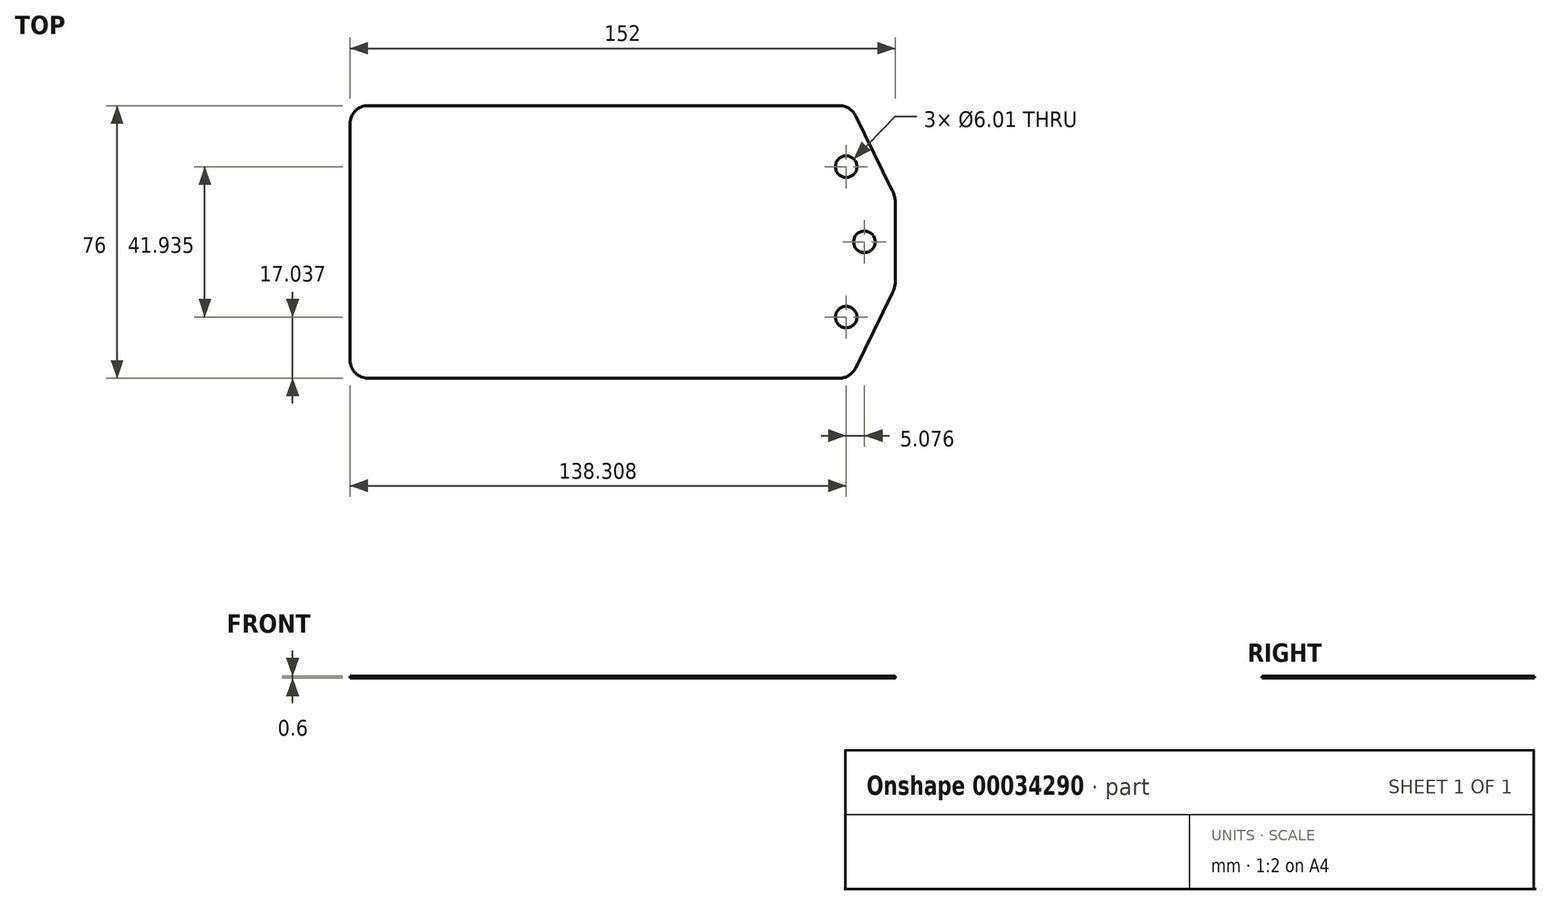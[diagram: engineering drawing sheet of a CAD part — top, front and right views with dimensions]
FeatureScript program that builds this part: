
annotation { "Feature Type Name" : "Feature", "Feature Type Description" : "" }
export const myFeature = defineFeature(function(context is Context, id is Id, definition is map)
    precondition{}
    {
        {
            var Q0;
            Q0=qCreatedBy(makeId("Top.planeOp"),FACE);
            var sketch = newSketch(context, id + "F0", { "sketchPlane" : qUnion([Q0])});
            skLineSegment(sketch, "E0.top", {"start": v(-72.18, -41.45) * mm, "end": v(59.23, -41.45) * mm});
            skLineSegment(sketch, "E0.left", {"start": v(-77.18, -3.45) * mm, "end": v(-77.18, -36.45) * mm});
            skPoint(sketch, "E1", {"position": v(62.34, -41.45) * mm});
            skPoint(sketch, "E2", {"position": v(74.82, -16.11) * mm});
            skPoint(sketch, "E3", {"position": v(-77.18, -3.45) * mm});
            skLineSegment(sketch, "E4", {"start": v(-77.18, -3.45) * mm, "end": v(92.62, -3.45) * mm, "construction": true});
            skLineSegment(sketch, "E5", {"start": v(63.72, -38.65) * mm, "end": v(74, -17.78) * mm});
            skLineSegment(sketch, "E6", {"start": v(74.82, -14.25) * mm, "end": v(74.82, -3.45) * mm});
            skPoint(sketch, "E7.visualSharp", {"position": v(-77.18, -41.45) * mm});
            skArc(sketch, "E7.filletArc", {"start": v(-77.18, -36.45) * mm, "mid": v(-75.72, -39.98) * mm, "end": v(-72.18, -41.45) * mm});
            skArc(sketch, "E8.filletArc", {"start": v(59.23, -41.45) * mm, "mid": v(61.87, -40.7) * mm, "end": v(63.72, -38.65) * mm});
            skArc(sketch, "E9.filletArc", {"start": v(74, -17.78) * mm, "mid": v(74.6, -16.06) * mm, "end": v(74.82, -14.25) * mm});
            skPoint(sketch, "E10", {"position": v(68.86, -28.22) * mm});
            skLineSegment(sketch, "E11", {"start": v(68.86, -28.22) * mm, "end": v(38.43, -13.23) * mm, "construction": true});
            skCircle(sketch, "E12", {"center": v(61.13, -24.41) * mm, "radius": 3 * mm});
            skCircle(sketch, "E13", {"center": v(66.2, -3.45) * mm, "radius": 3 * mm});
            skLineSegment(sketch, "E14.MirrorCS", {"start": v(-77.18, -3.45) * mm, "end": v(-77.18, 29.55) * mm});
            skArc(sketch, "E15.MirrorCS", {"start": v(-77.18, 29.55) * mm, "mid": v(-75.72, 33.09) * mm, "end": v(-72.18, 34.55) * mm});
            skLineSegment(sketch, "E16.MirrorCS", {"start": v(-72.18, 34.55) * mm, "end": v(59.23, 34.55) * mm});
            skArc(sketch, "E17.MirrorCS", {"start": v(59.23, 34.55) * mm, "mid": v(61.87, 33.8) * mm, "end": v(63.72, 31.76) * mm});
            skLineSegment(sketch, "E18.MirrorCS", {"start": v(63.72, 31.76) * mm, "end": v(74, 10.9) * mm});
            skCircle(sketch, "E19.MirrorC", {"center": v(61.13, 17.52) * mm, "radius": 3 * mm});
            skArc(sketch, "E20.MirrorCS", {"start": v(74, 10.9) * mm, "mid": v(74.6, 9.17) * mm, "end": v(74.82, 7.36) * mm});
            skLineSegment(sketch, "E21.MirrorCS", {"start": v(74.82, 7.36) * mm, "end": v(74.82, -3.45) * mm});
            skSolve(sketch);
        }
        {
            var Q0;
            Q0 = qSketchRegion(id + "F0", true);
            extrude(context, id + "F1", {"entities" : qUnion([Q0]), "depth" : 0.6 * mm});
        }
    });
